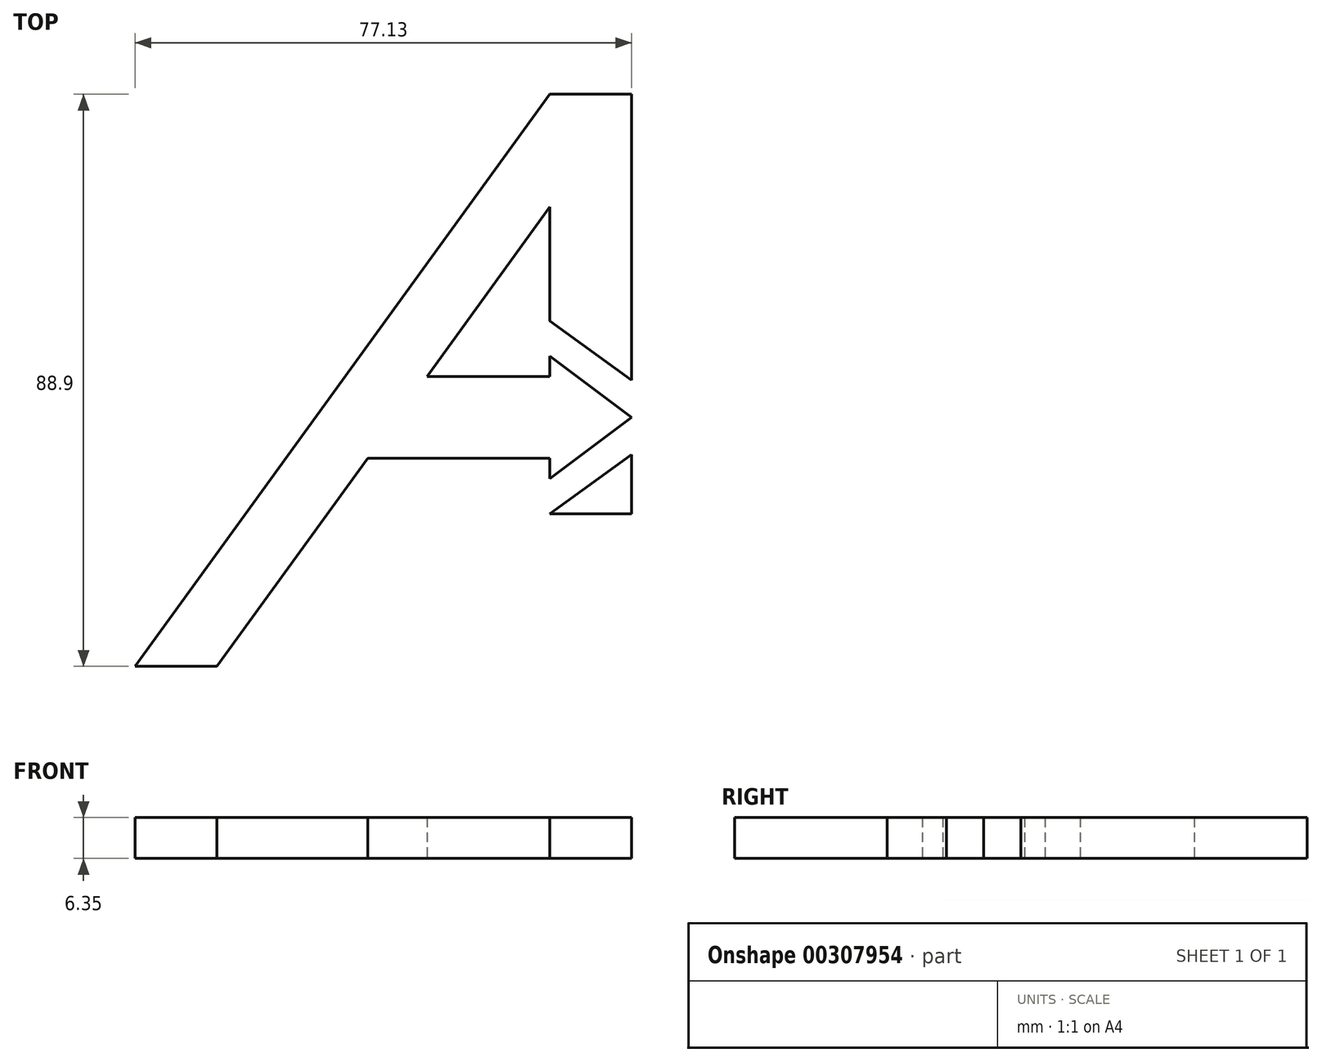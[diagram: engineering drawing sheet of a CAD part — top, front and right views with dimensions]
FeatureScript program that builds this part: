
annotation { "Feature Type Name" : "Feature", "Feature Type Description" : "" }
export const myFeature = defineFeature(function(context is Context, id is Id, definition is map)
    precondition{}
    {
        {
            var Q0;
            Q0=qCreatedBy(makeId("Top.planeOp"),FACE);
            var sketch = newSketch(context, id + "F0", { "sketchPlane" : qUnion([Q0])});
            skLineSegment(sketch, "E0.bottom", {"start": v(13.1, 50.23) * mm, "end": v(25.8, 50.23) * mm, "construction": true});
            skLineSegment(sketch, "E1", {"start": v(13.1, 50.23) * mm, "end": v(-51.33, -38.67) * mm, "construction": true});
            skLineSegment(sketch, "E2", {"start": v(-38.63, -38.67) * mm, "end": v(-51.33, -38.67) * mm, "construction": true});
            skLineSegment(sketch, "E3", {"start": v(13.1, 9.53) * mm, "end": v(25.8, 0) * mm, "construction": true});
            skLineSegment(sketch, "E4.MirrorCS", {"start": v(13.1, -9.53) * mm, "end": v(25.8, 0) * mm, "construction": true});
            skLineSegment(sketch, "E5", {"start": v(13.1, -9.53) * mm, "end": v(25.8, -9.52) * mm, "construction": true});
            skLineSegment(sketch, "E6", {"start": v(13.1, 9.53) * mm, "end": v(13.1, 6.35) * mm, "construction": true});
            skLineSegment(sketch, "E7", {"start": v(13.1, 6.35) * mm, "end": v(-6, 6.35) * mm, "construction": true});
            skLineSegment(sketch, "E8.MirrorCS", {"start": v(13.1, -6.35) * mm, "end": v(-6, -6.35) * mm, "construction": true});
            skLineSegment(sketch, "E9", {"start": v(13.1, -6.35) * mm, "end": v(-15.2, -6.35) * mm, "construction": true});
            skLineSegment(sketch, "E10", {"start": v(-51.33, -38.67) * mm, "end": v(-38.63, -38.67) * mm});
            skLineSegment(sketch, "E11", {"start": v(-15.2, -6.35) * mm, "end": v(13.1, -6.35) * mm});
            skLineSegment(sketch, "E12", {"start": v(13.1, -9.53) * mm, "end": v(25.8, 0) * mm});
            skLineSegment(sketch, "E13", {"start": v(-51.33, -38.67) * mm, "end": v(-28.52, -7.2) * mm});
            skLineSegment(sketch, "E14", {"start": v(-28.52, -7.2) * mm, "end": v(13.1, 50.23) * mm});
            skLineSegment(sketch, "E15", {"start": v(13.1, 50.23) * mm, "end": v(25.8, 50.23) * mm});
            skLineSegment(sketch, "E16", {"start": v(25.8, 50.23) * mm, "end": v(25.8, 5.78) * mm});
            skLineSegment(sketch, "E17", {"start": v(25.8, 5.78) * mm, "end": v(13.1, 14.99) * mm});
            skLineSegment(sketch, "E18", {"start": v(13.1, 14.99) * mm, "end": v(13.1, 32.7) * mm});
            skLineSegment(sketch, "E19", {"start": v(13.1, 32.7) * mm, "end": v(-6, 6.35) * mm});
            skLineSegment(sketch, "E20", {"start": v(13.1, 6.35) * mm, "end": v(13.1, 9.53) * mm});
            skLineSegment(sketch, "E21", {"start": v(25.8, 0) * mm, "end": v(13.1, 9.53) * mm});
            skLineSegment(sketch, "E22", {"start": v(13.1, 6.35) * mm, "end": v(-6, 6.35) * mm});
            skLineSegment(sketch, "E23", {"start": v(-15.2, -6.35) * mm, "end": v(-38.63, -38.67) * mm});
            skPoint(sketch, "E24.endSnap0", {"position": v(19.45, -4.76) * mm});
            skLineSegment(sketch, "E25", {"start": v(25.8, -14.99) * mm, "end": v(13.1, -14.99) * mm});
            skLineSegment(sketch, "E26.MirrorCS", {"start": v(25.8, -5.78) * mm, "end": v(13.1, -14.99) * mm});
            skLineSegment(sketch, "E27", {"start": v(13.1, -14.99) * mm, "end": v(25.8, -14.99) * mm});
            skLineSegment(sketch, "E28", {"start": v(25.8, -5.78) * mm, "end": v(25.8, -14.99) * mm});
            skLineSegment(sketch, "E29", {"start": v(13.1, -6.35) * mm, "end": v(13.1, -9.53) * mm});
            skSolve(sketch);
        }
        {
            var Q0;
            Q0=makeQuery(id+"F0.imprint","IMPRINT",FACE,{"disambiguationData":[TD([[makeQuery(id+"F0.imprint","IMPRINT",EDGE,{"derivedFrom":sQuery(id+"F0.wireOp",EDGE,"E10")}),1.0]])]});
            var Q1;
            Q1=makeQuery(id+"F0.imprint","IMPRINT",FACE,{"disambiguationData":[TD([[makeQuery(id+"F0.imprint","IMPRINT",EDGE,{"derivedFrom":sQuery(id+"F0.wireOp",EDGE,"E26.MirrorCS")}),1.0]])]});
            extrude(context, id + "F1", {"entities" : qUnion([Q0, Q1]), "depth" : 6.35 * mm});
        }
    });
